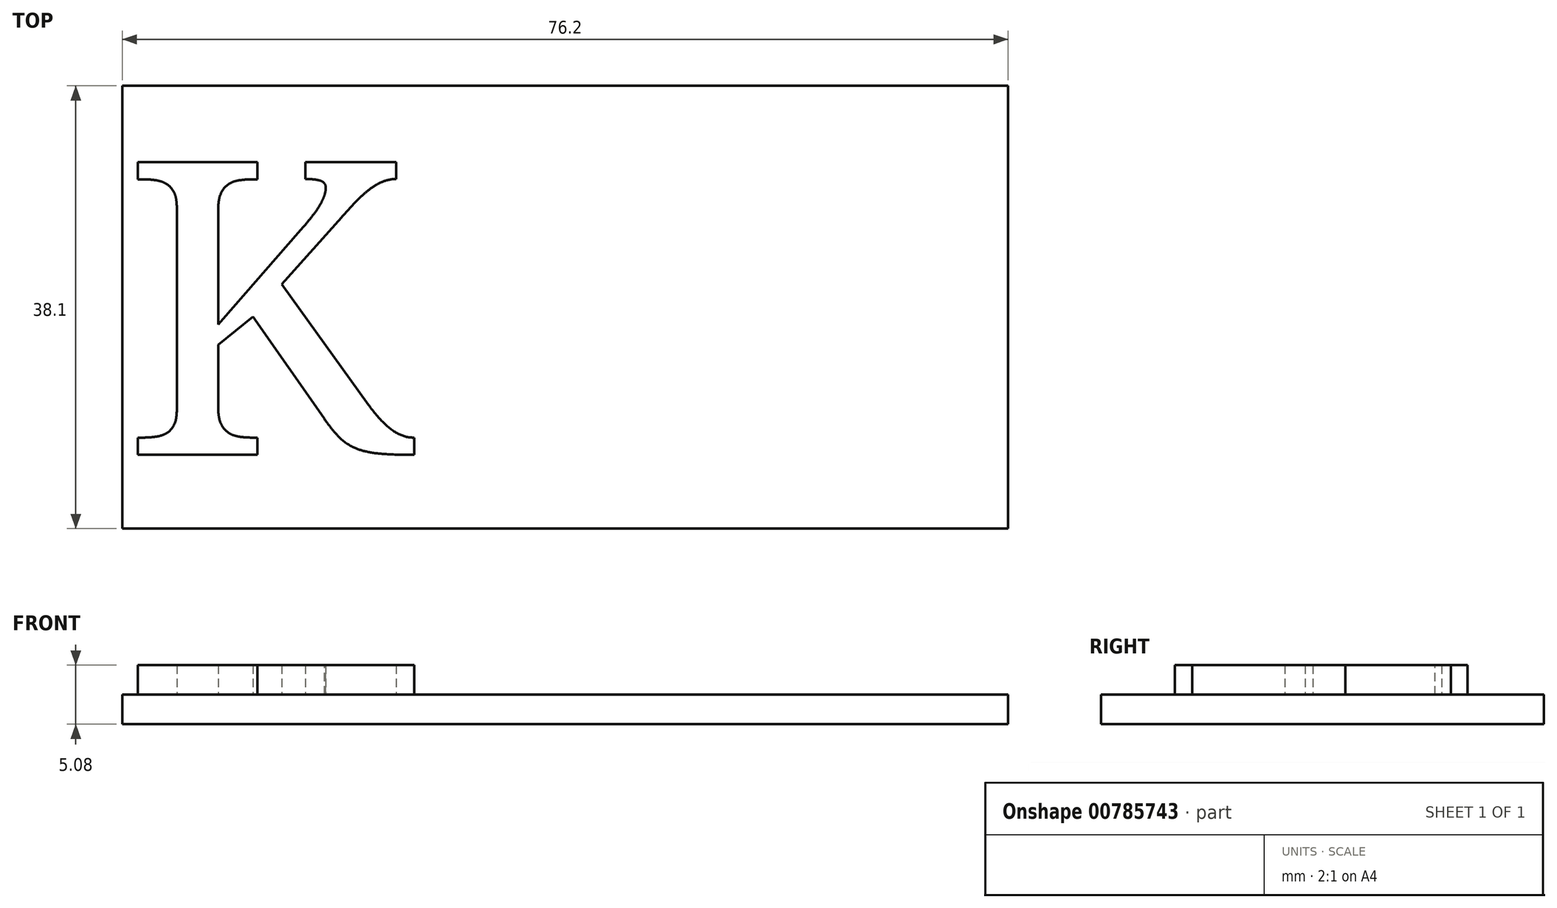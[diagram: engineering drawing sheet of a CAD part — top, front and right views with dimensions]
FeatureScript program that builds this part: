
annotation { "Feature Type Name" : "Feature", "Feature Type Description" : "" }
export const myFeature = defineFeature(function(context is Context, id is Id, definition is map)
    precondition{}
    {
        {
            var Q0;
            Q0=qCreatedBy(makeId("Top.planeOp"),FACE);
            var sketch = newSketch(context, id + "F0", { "sketchPlane" : qUnion([Q0])});
            skLineSegment(sketch, "E0.bottom", {"start": v(-38.1, 19.05) * mm, "end": v(38.1, 19.05) * mm});
            skLineSegment(sketch, "E0.top", {"start": v(-38.1, -19.05) * mm, "end": v(38.1, -19.05) * mm});
            skLineSegment(sketch, "E0.left", {"start": v(-38.1, 19.05) * mm, "end": v(-38.1, -19.05) * mm});
            skLineSegment(sketch, "E0.right", {"start": v(38.1, 19.05) * mm, "end": v(38.1, -19.05) * mm});
            skLineSegment(sketch, "E1", {"start": v(-38.1, 0) * mm, "end": v(38.1, 0) * mm, "construction": true});
            skLineSegment(sketch, "E2", {"start": v(38.1, 0) * mm, "end": v(0, 19.05) * mm, "construction": true});
            skLineSegment(sketch, "E3", {"start": v(0, 19.05) * mm, "end": v(0, -19.05) * mm, "construction": true});
            skPoint(sketch, "E4", {"position": v(0, 0) * mm});
            skSolve(sketch);
        }
        {
            var Q0;
            Q0=makeQuery(id+"F0.imprint","IMPRINT",FACE,{"disambiguationData":[TD([[makeQuery(id+"F0.imprint","IMPRINT",EDGE,{"derivedFrom":sQuery(id+"F0.wireOp",EDGE,"E0.bottom")}),-1.0]])]});
            extrude(context, id + "F1", {"entities" : qUnion([Q0]), "depth" : 2.54 * mm, "offsetDistance" : 25.4 * mm});
        }
        {
            var Q0;
            Q0=makeQuery(id+"F1.opExtrude","CAP_FACE",FACE,{"disambiguationData":[OSD([sQuery(id+"F0.wireOp",EDGE,"E0.bottom"),sQuery(id+"F0.wireOp",EDGE,"E0.top"),sQuery(id+"F0.wireOp",EDGE,"E0.left"),sQuery(id+"F0.wireOp",EDGE,"E0.right")])],"isStart":false});
            var sketch = newSketch(context, id + "F2", { "sketchPlane" : qUnion([Q0])});
            skLineSegment(sketch, "E5.bottom", {"start": v(38.1, 19.05) * mm, "end": v(-38.1, 19.05) * mm, "construction": true});
            skLineSegment(sketch, "E5.top", {"start": v(38.1, -19.05) * mm, "end": v(-38.1, -19.05) * mm, "construction": true});
            skLineSegment(sketch, "E5.left", {"start": v(38.1, 19.05) * mm, "end": v(38.1, -19.05) * mm, "construction": true});
            skLineSegment(sketch, "E5.right", {"start": v(-38.1, 19.05) * mm, "end": v(-38.1, -19.05) * mm, "construction": true});
            skPoint(sketch, "E5.middle", {"position": v(0, 0) * mm});
            skText(sketch, "E6", { "text": "K", "fontName": "NotoSerif-Regular.ttf"});
            skLineSegment(sketch, "E7", {"start": v(0, 0) * mm, "end": v(-38.1, 0) * mm, "construction": true});
            skPoint(sketch, "E8", {"position": v(-19.05, 0) * mm});
            skLineSegment(sketch, "E9", {"start": v(-19.05, 0) * mm, "end": v(-38.1, 0) * mm, "construction": true});
            skPoint(sketch, "E10", {"position": v(-28.58, 0) * mm});
            skLineSegment(sketch, "E11", {"start": v(-38.1, 0) * mm, "end": v(-10.7, 0) * mm, "construction": true});
            skLineSegment(sketch, "E12", {"start": v(-10.7, 0) * mm, "end": v(-24.4, 12.7) * mm, "construction": true});
            skPoint(sketch, "E13", {"position": v(-24.4, 0) * mm});
            const initialGuessF2  = {"E6": [-0.0381, -0.0127, 1, 0, 0.0254]};
            skSetInitialGuess(sketch, initialGuessF2);
            skSolve(sketch);
        }
        {
            var Q0;
            Q0 = qSketchRegion(id + "F2", true);
            extrude(context, id + "F3", {"entities" : qUnion([Q0]), "operationType" : NewBodyOperationType.ADD, "depth" : 2.54 * mm, "offsetDistance" : 25.4 * mm});
        }
    });
